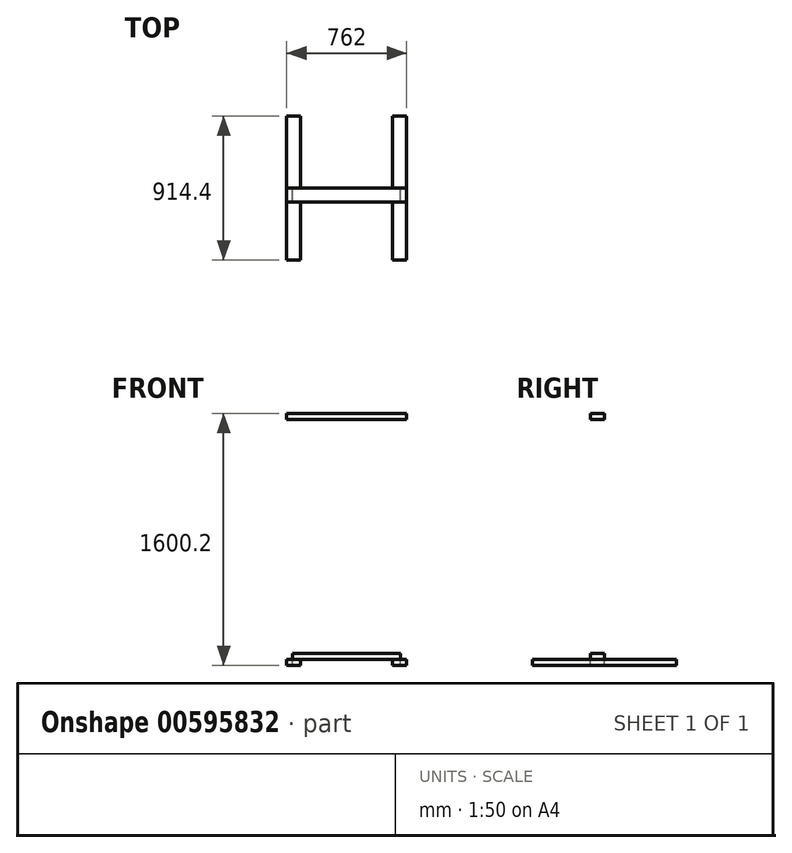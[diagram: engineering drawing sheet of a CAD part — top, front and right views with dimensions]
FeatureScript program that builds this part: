
annotation { "Feature Type Name" : "Feature", "Feature Type Description" : "" }
export const myFeature = defineFeature(function(context is Context, id is Id, definition is map)
    precondition{}
    {
        {
            var Q0;
            Q0=qCreatedBy(makeId("Front.planeOp"),FACE);
            var sketch = newSketch(context, id + "F0", { "sketchPlane" : qUnion([Q0])});
            skLineSegment(sketch, "E0.bottom", {"start": v(0, 0) * mm, "end": v(762, 0) * mm});
            skLineSegment(sketch, "E0.top", {"start": v(0, 38.1) * mm, "end": v(762, 38.1) * mm});
            skLineSegment(sketch, "E0.left", {"start": v(0, 0) * mm, "end": v(0, 38.1) * mm});
            skLineSegment(sketch, "E0.right", {"start": v(762, 0) * mm, "end": v(762, 38.1) * mm});
            skLineSegment(sketch, "E1.bottom", {"start": v(0, 0) * mm, "end": v(38.1, 0) * mm});
            skLineSegment(sketch, "E1.top", {"start": v(0, -1524) * mm, "end": v(38.1, -1524) * mm});
            skLineSegment(sketch, "E1.left", {"start": v(0, 0) * mm, "end": v(0, -1524) * mm});
            skLineSegment(sketch, "E1.right", {"start": v(38.1, 0) * mm, "end": v(38.1, -1524) * mm});
            skLineSegment(sketch, "E2.bottom", {"start": v(762, 0) * mm, "end": v(723.9, 0) * mm});
            skLineSegment(sketch, "E2.top", {"start": v(762, -1524) * mm, "end": v(723.9, -1524) * mm});
            skLineSegment(sketch, "E2.left", {"start": v(762, 0) * mm, "end": v(762, -1524) * mm});
            skLineSegment(sketch, "E2.right", {"start": v(723.9, 0) * mm, "end": v(723.9, -1524) * mm});
            skLineSegment(sketch, "E3.bottom", {"start": v(38.1, -1524) * mm, "end": v(723.9, -1524) * mm});
            skLineSegment(sketch, "E3.top", {"start": v(38.1, -1485.9) * mm, "end": v(723.9, -1485.9) * mm});
            skLineSegment(sketch, "E3.left", {"start": v(38.1, -1524) * mm, "end": v(38.1, -1485.9) * mm});
            skLineSegment(sketch, "E3.right", {"start": v(723.9, -1524) * mm, "end": v(723.9, -1485.9) * mm});
            skSolve(sketch);
        }
        {
            var Q0;
            Q0=makeQuery(id+"F0.imprint","IMPRINT",FACE,{"disambiguationData":[TD([[makeQuery(id+"F0.imprint","IMPRINT",EDGE,{"derivedFrom":sQuery(id+"F0.wireOp",EDGE,"E0.bottom")}),1.0]])]});
            var Q1;
            Q1=makeQuery(id+"F0.imprint","IMPRINT",FACE,{"disambiguationData":[TD([[makeQuery(id+"F0.imprint","IMPRINT",EDGE,{"derivedFrom":sQuery(id+"F0.wireOp",EDGE,"E1.bottom")}),-1.0]])]});
            var Q2;
            Q2=makeQuery(id+"F0.imprint","IMPRINT",FACE,{"disambiguationData":[TD([[makeQuery(id+"F0.imprint","IMPRINT",EDGE,{"derivedFrom":sQuery(id+"F0.wireOp",EDGE,"E2.bottom")}),1.0]])]});
            var Q3;
            Q3=makeQuery(id+"F0.imprint","IMPRINT",FACE,{"disambiguationData":[TD([[makeQuery(id+"F0.imprint","IMPRINT",EDGE,{"derivedFrom":sQuery(id+"F0.wireOp",EDGE,"E3.bottom")}),1.0]])]});
            extrude(context, id + "F1", {"entities" : qUnion([Q0, Q1, Q2, Q3]), "depth" : 88.9 * mm, "offsetDistance" : 25.4 * mm});
        }
        {
            var Q0;
            Q0=makeQuery(id+"F1.opExtrude","SWEPT_FACE",FACE,{"disambiguationData":[OSD([sQuery(id+"F0.wireOp",EDGE,"E1.top"),sQuery(id+"F0.wireOp",EDGE,"E2.top"),sQuery(id+"F0.wireOp",EDGE,"E3.bottom")])]});
            var sketch = newSketch(context, id + "F2", { "sketchPlane" : qUnion([Q0])});
            skLineSegment(sketch, "E4.bottom", {"start": v(0, -457.2) * mm, "end": v(88.9, -457.2) * mm});
            skLineSegment(sketch, "E4.top", {"start": v(0, 457.2) * mm, "end": v(88.9, 457.2) * mm});
            skLineSegment(sketch, "E4.left", {"start": v(0, -457.2) * mm, "end": v(0, 457.2) * mm});
            skLineSegment(sketch, "E4.right", {"start": v(88.9, -457.2) * mm, "end": v(88.9, 457.2) * mm});
            skLineSegment(sketch, "E5.bottom", {"start": v(762, -457.2) * mm, "end": v(673.1, -457.2) * mm});
            skLineSegment(sketch, "E5.top", {"start": v(762, 457.2) * mm, "end": v(673.1, 457.2) * mm});
            skLineSegment(sketch, "E5.left", {"start": v(762, -457.2) * mm, "end": v(762, 457.2) * mm});
            skLineSegment(sketch, "E5.right", {"start": v(673.1, -457.2) * mm, "end": v(673.1, 457.2) * mm});
            skSolve(sketch);
        }
        {
            var Q0;
            {var subQ0=sQuery(id+"F2.wireOp",EDGE,"E4.top");Q0=makeQuery(id+"F2.imprint","IMPRINT",FACE,{"disambiguationData":[TD([[makeQuery(id+"F2.imprint","IMPRINT",EDGE,{"derivedFrom":subQ0}),-1.0]])]});}
            var Q1;
            {var subQ0=sQuery(id+"F2.wireOp",EDGE,"E4.bottom");Q1=makeQuery(id+"F2.imprint","IMPRINT",FACE,{"disambiguationData":[TD([[makeQuery(id+"F2.imprint","IMPRINT",EDGE,{"derivedFrom":subQ0}),1.0]])]});}
            var Q2;
            {var subQ0=sQuery(id+"F2.wireOp",EDGE,"E4.left");var subQ1=sQuery(id+"F0.wireOp",EDGE,"E3.bottom");var subQ2=sQuery(id+"F0.wireOp",EDGE,"E2.top");var subQ3=sQuery(id+"F0.wireOp",EDGE,"E1.top");var subQ4=makeQuery(id+"F1.opExtrude","CAP_EDGE",EDGE,{"disambiguationData":[OSD([subQ3,subQ2,subQ1])],"isStart":true});var subQ5=makeQuery(id+"F2.imprint","INTERSECT",VERTEX,{"derivedFrom":[subQ4,subQ0]});var subQ6=makeQuery(id+"F1.opExtrude","CAP_EDGE",EDGE,{"disambiguationData":[OSD([subQ3,subQ2,subQ1])],"isStart":false});var subQ7=makeQuery(id+"F2.imprint","INTERSECT",VERTEX,{"derivedFrom":[subQ6,subQ0]});Q2=makeQuery(id+"F2.imprint","IMPRINT",FACE,{"disambiguationData":[TD([[makeQuery(id+"F2.imprint","IMPRINT",EDGE,{"disambiguationData":[TD([[subQ5,1.0],[subQ7,-1.0]])],"derivedFrom":subQ0}),1.0]])]});}
            var Q3;
            {var subQ0=sQuery(id+"F2.wireOp",EDGE,"E5.bottom");Q3=makeQuery(id+"F2.imprint","IMPRINT",FACE,{"disambiguationData":[TD([[makeQuery(id+"F2.imprint","IMPRINT",EDGE,{"derivedFrom":subQ0}),-1.0]])]});}
            var Q4;
            {var subQ0=sQuery(id+"F2.wireOp",EDGE,"E5.left");var subQ1=sQuery(id+"F0.wireOp",EDGE,"E3.bottom");var subQ2=sQuery(id+"F0.wireOp",EDGE,"E2.top");var subQ3=sQuery(id+"F0.wireOp",EDGE,"E1.top");var subQ4=makeQuery(id+"F1.opExtrude","CAP_EDGE",EDGE,{"disambiguationData":[OSD([subQ3,subQ2,subQ1])],"isStart":true});var subQ5=makeQuery(id+"F2.imprint","INTERSECT",VERTEX,{"derivedFrom":[subQ4,subQ0]});var subQ6=makeQuery(id+"F1.opExtrude","CAP_EDGE",EDGE,{"disambiguationData":[OSD([subQ3,subQ2,subQ1])],"isStart":false});var subQ7=makeQuery(id+"F2.imprint","INTERSECT",VERTEX,{"derivedFrom":[subQ6,subQ0]});Q4=makeQuery(id+"F2.imprint","IMPRINT",FACE,{"disambiguationData":[TD([[makeQuery(id+"F2.imprint","IMPRINT",EDGE,{"disambiguationData":[TD([[subQ5,1.0],[subQ7,-1.0]])],"derivedFrom":subQ0}),-1.0]])]});}
            var Q5;
            {var subQ0=sQuery(id+"F2.wireOp",EDGE,"E5.top");Q5=makeQuery(id+"F2.imprint","IMPRINT",FACE,{"disambiguationData":[TD([[makeQuery(id+"F2.imprint","IMPRINT",EDGE,{"derivedFrom":subQ0}),1.0]])]});}
            extrude(context, id + "F3", {"entities" : qUnion([Q0, Q1, Q2, Q3, Q4, Q5]), "depth" : 38.1 * mm, "offsetDistance" : 25.4 * mm});
        }
    });
